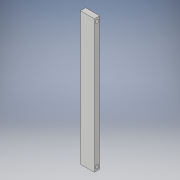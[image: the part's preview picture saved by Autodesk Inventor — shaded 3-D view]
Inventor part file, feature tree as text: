
AUTODESK INVENTOR PART (.ipt)
format: ipt  version: 2017 (Build 210142000, 142)  size: 98,816 bytes
history: native  units: in
note: dims shown in document units (in); Inventor stores cm internally (conversion verified against a paired STEP export)
features: extrude x1, sketch x1
ambient origin geometry x8: Origin, YZ Plane, XZ Plane, XY Plane, X Axis, Y Axis, Z Axis, Center Point
bodies: Solid1 (feature_tree)
feature tree (2):
  extrude  "Extrusion1"  Depth=0.75in
  sketch  "Sketch1"  dims[d0=19.0in d1=0.75in d2=0.5in d3=0.5in d4=0.5in d5=0.5in d6=2.0in d7=0.0in]
